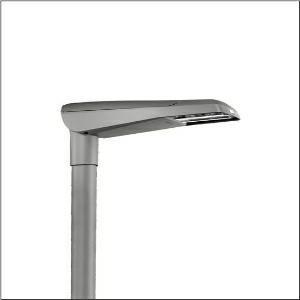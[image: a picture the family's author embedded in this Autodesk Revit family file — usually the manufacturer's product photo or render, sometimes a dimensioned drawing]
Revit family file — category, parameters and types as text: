
# Revit family: streetlight_sl_11_iq_micro___st1_0a_5xc1mc1f08de_be1f
name_source: partatom
category: Lighting Fixtures
units: mm (PartAtom-declared; Revit-internal decimal feet)

## family parameters
Cut with Voids When Loaded = No
Host = Face
Light Source = No
Part Type = Normal
Room Calculation Point = No
Round Connector Dimension = Use Diameter
Shared = No

## types (1)
- --- (1 x LED, 3740 lm, 27.4 W, 4000K)
    Apparent Load = 27 VA
    CIE Flux Codes = 33 66 96 100 100
    Color Rendering = 70
    Color Temperature = 4000K
    Default Elevation = 1800 mm
    Description = Streetlight SL 11 iQ micro, mast luminaire, primary light control with 3 zone facetted reflector, of plastic, silver coated, highly specular, primary optical cover: cover, of PMMA, transparent, light distribution: ST1.0a, light emission: direct distribution, primary light characteristic: asymmetric, installation type: post-top, side-entry, lamps: LED, High Power LED, rated values: 3.510lm | 27,7W | 126,7lm/W (begin service life); end service life: 3.510lm | 28,1W; at 50% lumin. flux: 1.755lm | 13,4W | 131lm/W, colour temperature: 2200/2700/3000/4000K, colour rendering: CRI > 70, light colour: 722/727/730/740, light setting 1 begin service life: 100% | 3.510lm | 27,7W | 126,7lm/W | 3.000K, light setting 1 end service life: 28,1W, further light settings possible, control: Street-Remote, Auto-Match, Temp-Guard, Lumen-Switch, Night-Set, Smart-Wire, Light-Fading, Desk-Remote (wireless, voltage-free reading and setting of iQ features in the workshop via application-optimized NFC function/RFID function), optimised constant luminous flux control (CLO 2.0), with cable H07RN-F 5x 1.5mm², mains connection: 220..240V, AC, 50/60Hz, connection cable pre-assembled, cable length: 6,5m, luminaire housing, of diecast aluminium, powder-coated, Siteco® metallic grey (DB 702S), please order mast flange separately, inclination adjustable without tools: 0°, 5°, 10°, 15° (post-top) | 0°, -5°, -10°, -15° (side-entry), sealing non-destructively replaceable, multi-level sealing system, length: 600mm, width: 174mm, height: 116mm, mast flange for spigot size: 42mm (side-entry): 5XC10008XM4, 60/48mm (side-entry/post-top): 5XC10108XM2, 76/60mm (side-entry/post-top): 5XC10108XM1, equipment: Power, protection rating (complete): IP66, insulation class (complete): insulation class II (safety insulation), certification: CE, ENEC, ENEC+, VDE, impact resistance: IK10, permissible operating ambient temperature for outdoor applications: -25..+50°C, standard-compliant lighting for roads and squares, Environmental Product Declaration (EPD) tested and certified by an independent institute, packaging unit: 1 piece

Light Distribution: ST1.0a
    Height = 116 mm
    Lamp = 1 x LED
    Lamp Light Flux = 3740 lm
    Lamp Power = 27.4 W
    Lamp count = 1
    Length = 600 mm
    Luminous efficacy = 137 lm/W
    Manufacturer = Siteco
    ModVariant = No
    Model = 5XC1MC1F08DE
    Number of Poles = 1
    OnlyDefault = Yes
    Power Factor = 1
    Product Name = Streetlight SL 11 iQ micro | ST1.0a
    Product group = mast luminaire | pylon top
    ProductGroupID = 6100
    Protection Class = Protection class II
    Protection Degree = IP 66
    RLX_Detail_Level = 1
    RLX_Emergency_Light_Flux = 0 lm
    RLX_Emergency_Type = 0
    RLX_Emergency_Type_DB = No
    RlxData = <blob elided: 58921 chars, md5=9bac3212>
    Socket = socket
    Standby Power = 0 W
    System Light Flux = 3740 lm
    System Power = 27 W
    Type Comments = individual setting: luminous flux: 100 % | dim-lin: 254 | 726 mA
    Type Image = l_1006566.jpg
    URL = http://relux.com
    VarID = @adj_041418
    Voltage = 0 V
    Weight = 0.00 kg
    Width = 174 mm

## geometry (parser evidence)
native form markers: Blend x4, Sweep x10
no freeform markers — native parametric forms only
